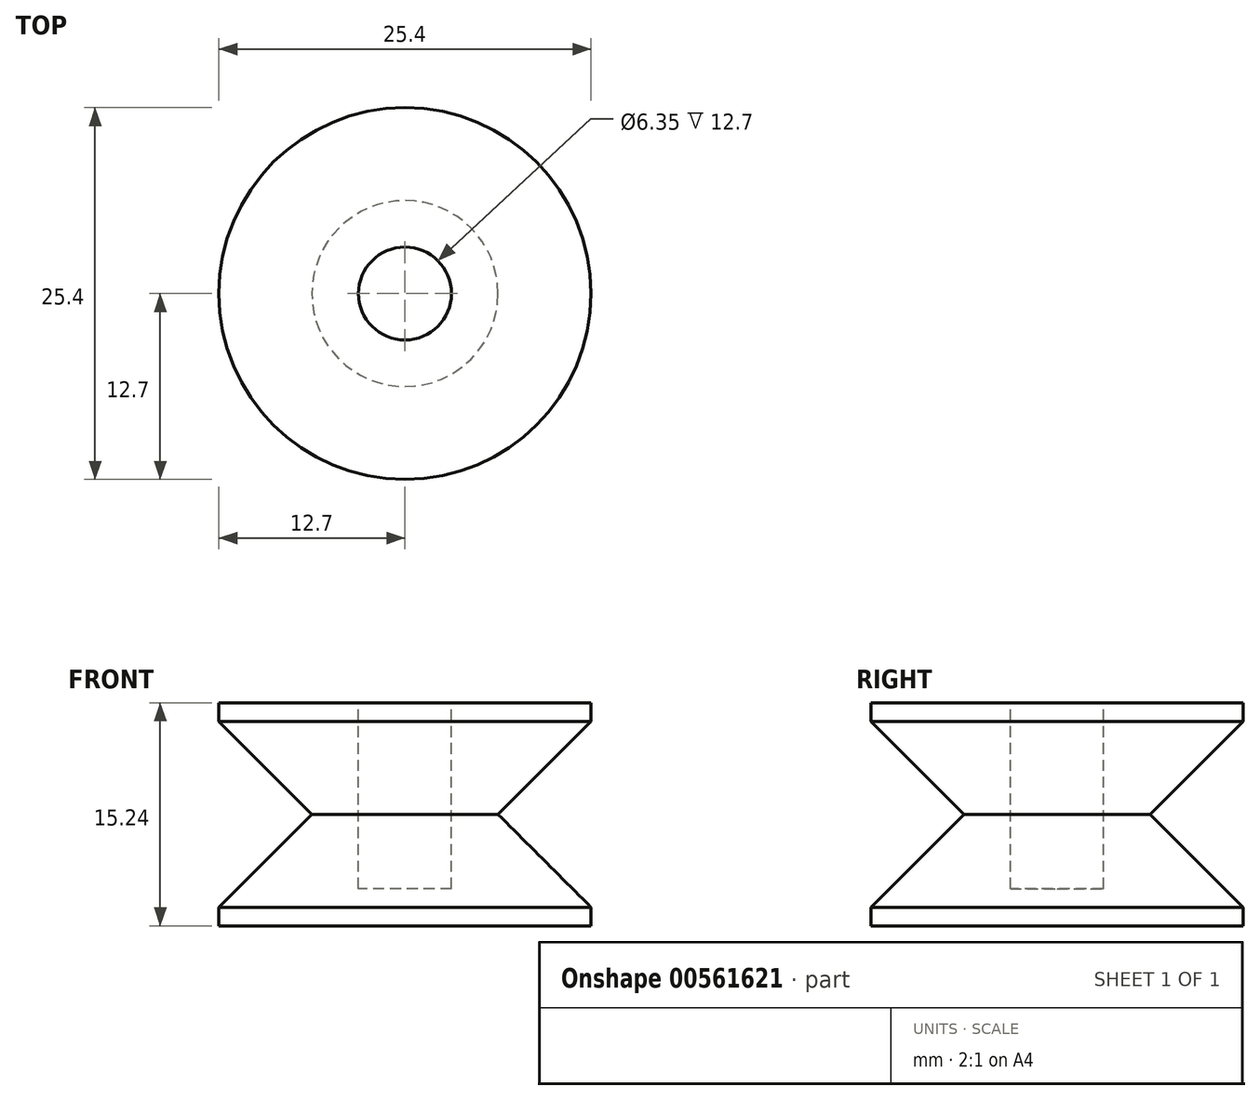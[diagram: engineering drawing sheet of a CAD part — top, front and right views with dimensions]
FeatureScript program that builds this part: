
annotation { "Feature Type Name" : "Feature", "Feature Type Description" : "" }
export const myFeature = defineFeature(function(context is Context, id is Id, definition is map)
    precondition{}
    {
        {
            var Q0;
            Q0=qCreatedBy(makeId("Front.planeOp"),FACE);
            var sketch = newSketch(context, id + "F0", { "sketchPlane" : qUnion([Q0])});
            skLineSegment(sketch, "E0", {"start": v(0, 16.14) * mm, "end": v(0, 3.44) * mm});
            skLineSegment(sketch, "E1", {"start": v(0, 3.44) * mm, "end": v(-6.35, 3.44) * mm});
            skLineSegment(sketch, "E2", {"start": v(-6.35, 3.44) * mm, "end": v(-12.7, 3.44) * mm});
            skLineSegment(sketch, "E3", {"start": v(-12.7, 3.44) * mm, "end": v(-6.35, 9.79) * mm});
            skPoint(sketch, "E3.endSnap0", {"position": v(0, 9.79) * mm});
            skLineSegment(sketch, "E4", {"start": v(-6.35, 9.79) * mm, "end": v(-12.7, 16.14) * mm});
            skLineSegment(sketch, "E5", {"start": v(-12.7, 16.14) * mm, "end": v(0, 16.14) * mm});
            skSolve(sketch);
        }
        {
            var Q0;
            Q0 = qSketchRegion(id + "F0", true);
            var Q1;
            Q1=sQuery(id+"F0.wireOp",EDGE,"E0");
            revolve(context, id + "F1", {"entities" : qUnion([Q0]), "axis" : qUnion([Q1]), "revolveType" : RevolveType.FULL});
        }
        {
            var Q0;
            Q0=makeQuery(id+"F1.opRevolve","SWEPT_FACE",FACE,{"disambiguationData":[OSD([sQuery(id+"F0.wireOp",EDGE,"E1"),sQuery(id+"F0.wireOp",EDGE,"E2")])]});
            var sketch = newSketch(context, id + "F2", { "sketchPlane" : qUnion([Q0])});
            skCircle(sketch, "E6", {"center": v(0, 0) * mm, "radius": 12.7 * mm});
            skSolve(sketch);
        }
        {
            var Q0;
            Q0 = qSketchRegion(id + "F2", true);
            extrude(context, id + "F3", {"entities" : qUnion([Q0]), "operationType" : NewBodyOperationType.ADD, "depth" : 1.27 * mm, "offsetDistance" : 25.4 * mm});
        }
        {
            var Q0;
            Q0=makeQuery(id+"F1.opRevolve","SWEPT_FACE",FACE,{"disambiguationData":[OSD([sQuery(id+"F0.wireOp",EDGE,"E5")])]});
            var sketch = newSketch(context, id + "F4", { "sketchPlane" : qUnion([Q0])});
            skCircle(sketch, "E7", {"center": v(0, 0) * mm, "radius": 12.7 * mm});
            skSolve(sketch);
        }
        {
            var Q0;
            Q0 = qSketchRegion(id + "F4", true);
            extrude(context, id + "F5", {"entities" : qUnion([Q0]), "operationType" : NewBodyOperationType.ADD, "depth" : 1.27 * mm, "offsetDistance" : 25.4 * mm});
        }
        {
            var Q0;
            Q0=makeQuery(id+"F5.opExtrude","CAP_FACE",FACE,{"disambiguationData":[OSD([sQuery(id+"F4.wireOp",EDGE,"E7")])],"isStart":false});
            var sketch = newSketch(context, id + "F6", { "sketchPlane" : qUnion([Q0])});
            skSolve(sketch);
        }
        {
            var Q0;
            Q0=makeQuery(id+"F6.imprint","IMPRINT",FACE,{"disambiguationData":[TD([[makeQuery(id+"F6.imprint","IMPRINT",EDGE,{"derivedFrom":makeQuery(id+"F5.opExtrude","CAP_EDGE",EDGE,{"disambiguationData":[OSD([sQuery(id+"F4.wireOp",EDGE,"E7")])],"isStart":false})}),1.0]])]});
            var sketch = newSketch(context, id + "F7", { "sketchPlane" : qUnion([Q0])});
            skCircle(sketch, "E8", {"center": v(0, 0) * mm, "radius": 3.18 * mm});
            skSolve(sketch);
        }
        {
            var Q0;
            Q0 = qSketchRegion(id + "F7", true);
            extrude(context, id + "F8", {"entities" : qUnion([Q0]), "operationType" : NewBodyOperationType.REMOVE, "oppositeDirection" : true, "depth" : 12.7 * mm, "offsetDistance" : 25.4 * mm});
        }
    });
